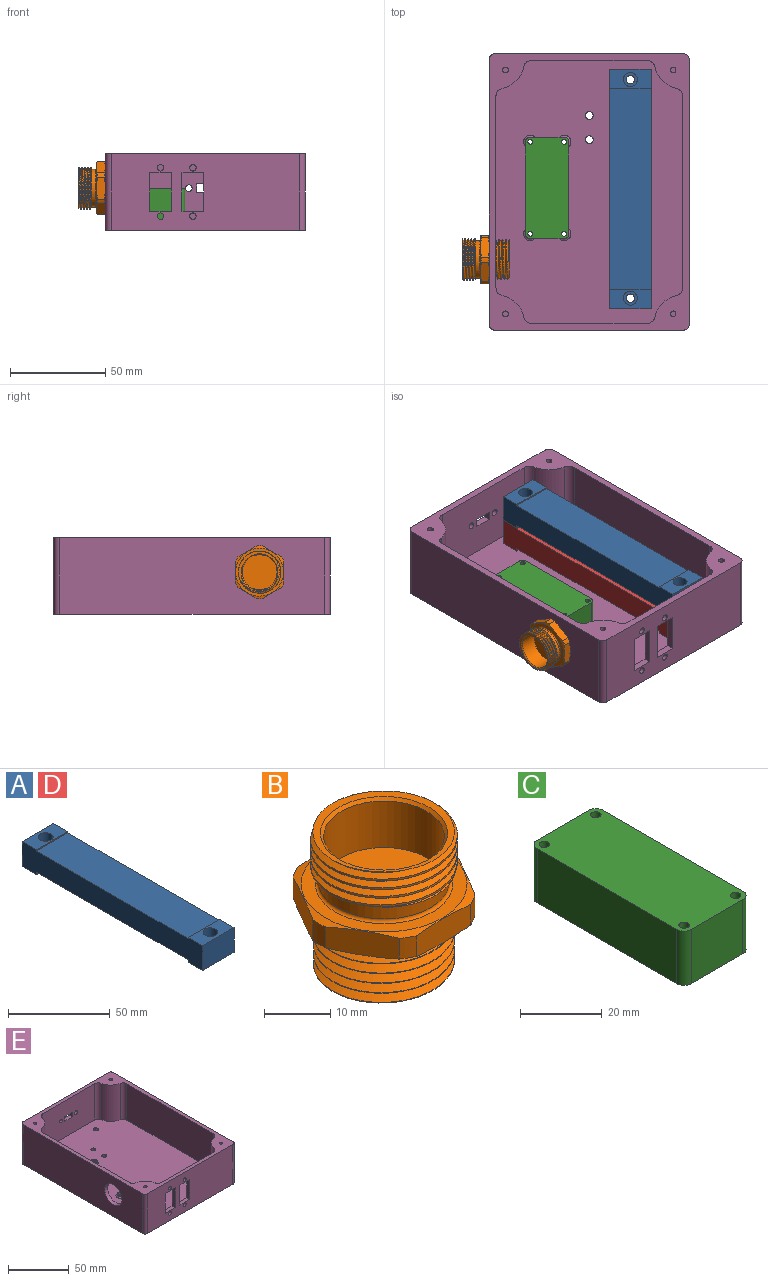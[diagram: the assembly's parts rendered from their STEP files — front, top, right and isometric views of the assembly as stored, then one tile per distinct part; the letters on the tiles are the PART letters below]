
ASSEMBLY  parts=5 mates=3
PART A: 20 faces, bbox 21.9x125.7x15 mm
  f0: plane 21.93x14.95mm, normal (0,-1,0), area 327.9mm2, adj f1,f11,f12,f13
  f1: plane 21.93x10mm, normal (0,0,-1), area 203.7mm2, adj f0,f2,f12,f13,f14
  f2: plane 21.93x1.5mm, normal (0,1,0), area 32.9mm2, adj f1,f3,f12,f13
  f3: plane 105.73x21.93mm, normal (0,0,-1), area 2318.7mm2, adj f2,f4,f12,f13
  f4: plane 21.93x1.5mm, normal (0,-1,0), area 32.9mm2, adj f3,f5,f12,f13
  f5: plane 21.93x10mm, normal (0,0,-1), area 203.7mm2, adj f4,f6,f12,f13,f17
  f6: plane 21.93x14.95mm, normal (0,1,0), area 327.9mm2, adj f5,f7,f12,f13
  f7: plane 21.93x10mm, normal (0,0,1), area 177.4mm2, adj f6,f8,f12,f13,f19
  f8: plane 21.93x0.68mm, normal (0,-1,0), area 14.9mm2, adj f7,f9,f12,f13
  f9: plane 105.73x21.93mm, normal (0,0,1), area 2318.7mm2, adj f8,f10,f12,f13
  f10: plane 21.93x0.68mm, normal (0,1,0), area 14.9mm2, adj f9,f11,f12,f13
  f11: plane 21.93x10mm, normal (0,0,1), area 177.4mm2, adj f0,f10,f12,f13,f16
  f12: plane 125.73x14.95mm, normal (-1,0,0), area 1649.2mm2, adj f0,f1,f2,f3,f4,f5,f6,f7
  f13: plane 125.73x14.95mm, normal (1,0,0), area 1649.2mm2, adj f0,f1,f2,f3,f4,f5,f6,f7
  f14: cylinder r=2.23mm len=4.45mm, axis (0,0,1), area 44mm2, adj f1,f15
  f15: plane 7.3x7.3mm, normal (0,0,1), area 26.3mm2, adj f14,f16
  f16: cylinder r=3.65mm len=11.8mm, axis (0,0,1), area 270.6mm2, adj f11,f15
  f17: cylinder r=2.23mm len=4.45mm, axis (0,0,1), area 44mm2, adj f5,f18
  f18: plane 7.3x7.3mm, normal (0,0,1), area 26.3mm2, adj f17,f19
  f19: cylinder r=3.65mm len=11.8mm, axis (0,0,1), area 270.6mm2, adj f7,f18
PART B: 37 faces, bbox 29x29x27.2 mm
  f0: cone r=9.14mm half-angle=45deg, axis (0,0,1), area 41.7mm2, adj f1,f11
  f1: cylinder r=9.14mm len=18.29mm, axis (0,0,1), area 494.7mm2, adj f0,f36
  f2: torus R=10.42mm, axis (0,0,-1), area 50.8mm2, adj f6,f10
  f3: cone r=12.57mm half-angle=75.1deg, axis (0,0,1), area 58.6mm2, adj f4,f16,f17,f18,f19,f20,f21,f22
  f4: cylinder r=13.97mm len=3.83mm, axis (0,0,1), area 10mm2, adj f3,f5,f18,f19
  f5: cone r=12.57mm half-angle=75.1deg, axis (0,0,-1), area 58.6mm2, adj f4,f10,f16,f17,f18,f19,f20,f21
  f6: cylinder r=9.91mm len=19.81mm, axis (0,0,-1), area 150mm2, adj f2,f15
  f7: cylinder r=11.11mm len=22.23mm, axis (0,0,-1), area 96.2mm2, adj f11,f13,f14,f15
  f8: cylinder r=10.67mm len=21.34mm, axis (0,0,1), area 91mm2, adj f9,f27,f28,f30,f31,f32,f33,f34
  f9: plane 21.1x21.07mm, normal (0,0,-1), area 313.4mm2, adj f8,f28,f29,f30
  f10: plane 25.15x25.15mm, normal (0,0,1), area 156mm2, adj f2,f5
  f11: plane 22.04x22mm, normal (0,0,1), area 67.3mm2, adj f0,f7,f12,f13,f14
  f12: cylinder r=10.16mm len=20.32mm, axis (0,0,-1), area 71.7mm2, adj f11,f13,f14,f15
  f13: bspline ~22.23x22.23mm, area 300.1mm2, adj f7,f11,f12,f15
  f14: bspline ~22.25x22.25mm, area 300.2mm2, adj f7,f11,f12,f15
  f15: plane 22.1x21.92mm, normal (0,0,-1), area 51.3mm2, adj f6,f7,f12,f13,f14
  f16: plane 10.08x5.82mm, normal (-0.87,-0.5,0), area 49.7mm2, adj f3,f5,f23,f26
  f17: plane 11.64x4.51mm, normal (0,-1,0), area 49.8mm2, adj f3,f5,f22,f23
  f18: plane 10.08x5.82mm, normal (0.87,-0.5,0), area 49.8mm2, adj f3,f4,f5,f22
  f19: plane 10.08x5.82mm, normal (0.87,0.5,0), area 49.8mm2, adj f3,f4,f5,f21
  f20: plane 11.64x4.51mm, normal (0,1,0), area 49.8mm2, adj f3,f5,f21,f25
  f21: cylinder r=13.97mm len=3.83mm, axis (0,0,1), area 10mm2, adj f3,f5,f19,f20
  f22: cylinder r=13.97mm len=3.83mm, axis (0,0,1), area 10mm2, adj f3,f5,f17,f18
  f23: cylinder r=13.97mm len=3.83mm, axis (0,0,1), area 10mm2, adj f3,f5,f16,f17
  f24: plane 10.08x5.82mm, normal (-0.87,0.5,0), area 49.8mm2, adj f3,f5,f25,f26
  f25: cylinder r=13.97mm len=3.83mm, axis (0,0,1), area 10mm2, adj f3,f5,f20,f24
  f26: cylinder r=13.97mm len=3.83mm, axis (0,0,1), area 10mm2, adj f3,f5,f16,f24
  f27: plane 25.15x25.15mm, normal (0,0,-1), area 139.2mm2, adj f3,f8,f31,f32,f35
  f28: bspline ~22.43x21.37mm, area 587.3mm2, adj f8,f9,f29,f31
  f29: bspline ~19.37x18.44mm, area 5mm2, adj f9,f28,f30,f33
  f30: bspline ~22.43x21.34mm, area 536.9mm2, adj f8,f9,f29,f34
  f31: plane 4.86x3.84mm, normal (0.34,0.37,-0.87), area 6.2mm2, adj f8,f27,f28,f32,f33,f35
  f32: plane 1.7x0.05mm, normal (-0.71,-0.7,0), area 0.1mm2, adj f8,f27,f31,f34,f35
  f33: plane 3.84x3.81mm, normal (0.71,0.7,-0.01), area 0.1mm2, adj f8,f29,f31,f34
  f34: plane 4.83x3.84mm, normal (0.37,0.34,0.87), area 6.2mm2, adj f8,f30,f32,f33
  f35: cylinder r=10.67mm len=0.75mm, axis (0,0,1), area 0mm2, adj f27,f31,f32
  f36: plane 18.29x18.29mm, normal (0,0,1), area 262.7mm2, adj f1
PART C: 14 faces, bbox 22.9x53.3x16.2 mm
  f0: plane 17.78x16.2mm, normal (0,1,0), area 288mm2, adj f1,f11,f12,f13
  f1: cylinder r=2.54mm len=16.2mm, axis (0,0,-1), area 64.6mm2, adj f0,f2,f12,f13
  f2: plane 48.26x16.2mm, normal (-1,0,0), area 781.8mm2, adj f1,f3,f12,f13
  f3: cylinder r=2.54mm len=16.2mm, axis (0,0,-1), area 64.6mm2, adj f2,f4,f12,f13
  f4: plane 17.78x16.2mm, normal (0,-1,0), area 288mm2, adj f3,f5,f12,f13
  f5: cylinder r=2.54mm len=16.2mm, axis (0,0,-1), area 64.6mm2, adj f4,f6,f12,f13
  f6: plane 48.26x16.2mm, normal (1,0,0), area 781.8mm2, adj f5,f11,f12,f13
  f7: cylinder r=1.27mm len=16.2mm, axis (0,0,-1), area 129.3mm2, adj f12,f13
  f8: cylinder r=1.27mm len=16.2mm, axis (0,0,-1), area 129.3mm2, adj f12,f13
  f9: cylinder r=1.27mm len=16.2mm, axis (0,0,-1), area 129.3mm2, adj f12,f13
  f10: cylinder r=1.27mm len=16.2mm, axis (0,0,-1), area 129.3mm2, adj f12,f13
  f11: cylinder r=2.54mm len=16.2mm, axis (0,0,-1), area 64.6mm2, adj f0,f6,f12,f13
  f12: plane 53.34x22.86mm, normal (0,0,1), area 1193.5mm2, adj f0,f1,f2,f3,f4,f5,f6,f7
  f13: plane 53.34x22.86mm, normal (0,0,-1), area 1193.5mm2, adj f0,f1,f2,f3,f4,f5,f6,f7
PART D: same geometry as A
PART E: 80 faces, bbox 105x145x40 mm
  f0: plane 60.85x36.5mm, normal (0,-1,0), area 2160.7mm2, adj f4,f6,f66,f69,f72,f73,f74,f75
  f1: plane 99x40mm, normal (0,1,0), area 3899.6mm2, adj f6,f10,f16,f17,f72,f73,f74,f75
  f2: plane 60.85x36.5mm, normal (0,1,0), area 1724.8mm2, adj f4,f6,f19,f20,f21,f22,f23,f24
  f3: plane 100.85x36.5mm, normal (-1,0,0), area 3681.1mm2, adj f4,f6,f63,f65
  f4: plane 138x98mm, normal (0,0,1), area 12582.2mm2, adj f0,f2,f3,f5,f11,f13,f32,f35
  f5: plane 100.85x36.5mm, normal (1,0,0), area 3366.9mm2, adj f4,f6,f67,f70,f71
  f6: plane 145x105mm, normal (0,0,1), area 2391.2mm2, adj f0,f1,f2,f3,f5,f7,f8,f9
  f7: plane 99x40mm, normal (0,-1,0), area 3463.7mm2, adj f6,f10,f15,f18,f19,f20,f21,f22
  f8: plane 139x40mm, normal (1,0,0), area 5560mm2, adj f6,f10,f15,f16
  f9: plane 139x40mm, normal (-1,0,0), area 5245.8mm2, adj f6,f10,f17,f18,f71
  f10: plane 145x105mm, normal (0,0,-1), area 14996.6mm2, adj f1,f7,f8,f9,f12,f14,f15,f16
  f11: cylinder r=2.25mm len=4.5mm, axis (0,0,-1), area 11.9mm2, adj f4,f12
  f12: cone r=2.25mm half-angle=41deg, axis (0,0,-1), area 75.3mm2, adj f10,f11
  f13: cylinder r=2.25mm len=4.5mm, axis (0,0,-1), area 11.9mm2, adj f4,f14
  f14: cone r=2.25mm half-angle=41deg, axis (0,0,-1), area 75.3mm2, adj f10,f13
  f15: cylinder r=3mm len=40mm, axis (0,0,1), area 188.5mm2, adj f6,f7,f8,f10
  f16: cylinder r=3mm len=40mm, axis (0,0,-1), area 188.5mm2, adj f1,f6,f8,f10
  f17: cylinder r=3mm len=40mm, axis (0,0,1), area 188.5mm2, adj f1,f6,f9,f10
  f18: cylinder r=3mm len=40mm, axis (0,0,-1), area 188.5mm2, adj f6,f7,f9,f10
  f19: cylinder r=1.7mm len=3.5mm, axis (0,-1,0), area 37.4mm2, adj f2,f7
  f20: cylinder r=1.7mm len=3.5mm, axis (0,-1,0), area 37.4mm2, adj f2,f7
  f21: cylinder r=1.7mm len=3.5mm, axis (0,-1,0), area 37.4mm2, adj f2,f7
  f22: cylinder r=1.7mm len=3.5mm, axis (0,-1,0), area 37.4mm2, adj f2,f7
  f23: plane 11.5x3.5mm, normal (0,0,-1), area 40.3mm2, adj f2,f7,f24,f25
  f24: plane 20x3.5mm, normal (-1,0,0), area 70mm2, adj f2,f7,f23,f26
  f25: plane 20x3.5mm, normal (1,0,0), area 70mm2, adj f2,f7,f23,f26
  f26: plane 11.5x3.5mm, normal (0,0,1), area 40.3mm2, adj f2,f7,f24,f25
  f27: plane 11.5x3.5mm, normal (0,0,-1), area 40.3mm2, adj f2,f7,f28,f29
  f28: plane 20x3.5mm, normal (-1,0,0), area 70mm2, adj f2,f7,f27,f30
  f29: plane 20x3.5mm, normal (1,0,0), area 70mm2, adj f2,f7,f27,f30
  f30: plane 11.5x3.5mm, normal (0,0,1), area 40.3mm2, adj f2,f7,f28,f29
  f31: cylinder r=1.5mm len=36.5mm, axis (0,0,1), area 344mm2, adj f6,f33
  f32: cylinder r=15mm len=36.5mm, axis (0,0,1), area 627.7mm2, adj f4,f6,f69,f70
  f33: plane 3x3mm, normal (0,0,1), area 7.1mm2, adj f31
  f34: cylinder r=1.5mm len=36.5mm, axis (0,0,1), area 344mm2, adj f6,f36
  f35: cylinder r=15mm len=36.5mm, axis (0,0,1), area 627.7mm2, adj f4,f6,f67,f68
  f36: plane 3x3mm, normal (0,0,1), area 7.1mm2, adj f34
  f37: cylinder r=1.5mm len=36.5mm, axis (0,0,1), area 344mm2, adj f6,f39
  f38: cylinder r=15mm len=36.5mm, axis (0,0,1), area 627.7mm2, adj f4,f6,f65,f66
  f39: plane 3x3mm, normal (0,0,1), area 7.1mm2, adj f37
  f40: cylinder r=1.5mm len=36.5mm, axis (0,0,1), area 344mm2, adj f6,f42
  f41: cylinder r=15mm len=36.5mm, axis (0,0,1), area 627.7mm2, adj f4,f6,f63,f64
  f42: plane 3x3mm, normal (0,0,1), area 7.1mm2, adj f40
  f43: cylinder r=2.54mm len=5.08mm, axis (0,0,-1), area 16mm2, adj f44,f51
  f44: plane 5.08x5.08mm, normal (0,0,1), area 13.7mm2, adj f43,f61
  f45: cylinder r=2.54mm len=5.08mm, axis (0,0,-1), area 16mm2, adj f46,f52
  f46: plane 5.08x5.08mm, normal (0,0,1), area 13.7mm2, adj f45,f59
  f47: cylinder r=2.54mm len=5.08mm, axis (0,0,-1), area 16mm2, adj f48,f53
  f48: plane 5.08x5.08mm, normal (0,0,1), area 13.7mm2, adj f47,f57
  f49: cylinder r=2.54mm len=5.08mm, axis (0,0,-1), area 16mm2, adj f50,f54
  f50: plane 5.08x5.08mm, normal (0,0,1), area 13.7mm2, adj f49,f55
  f51: torus R=3.54mm, axis (0,0,1), area 28.7mm2, adj f4,f43
  f52: torus R=3.54mm, axis (0,0,1), area 28.7mm2, adj f4,f45
  f53: torus R=3.54mm, axis (0,0,1), area 28.7mm2, adj f4,f47
  f54: torus R=3.54mm, axis (0,0,1), area 28.7mm2, adj f4,f49
  f55: cylinder r=1.45mm len=4.7mm, axis (0,0,-1), area 42.8mm2, adj f50,f56
  f56: cone r=1.45mm half-angle=45deg, axis (0,0,-1), area 13.2mm2, adj f10,f55
  f57: cylinder r=1.45mm len=4.7mm, axis (0,0,-1), area 42.8mm2, adj f48,f58
  f58: cone r=1.45mm half-angle=45deg, axis (0,0,-1), area 13.2mm2, adj f10,f57
  f59: cylinder r=1.45mm len=4.7mm, axis (0,0,-1), area 42.8mm2, adj f46,f60
  f60: cone r=1.45mm half-angle=45deg, axis (0,0,-1), area 13.2mm2, adj f10,f59
  f61: cylinder r=1.45mm len=4.7mm, axis (0,0,-1), area 42.8mm2, adj f44,f62
  f62: cone r=1.45mm half-angle=45deg, axis (0,0,-1), area 13.2mm2, adj f10,f61
  f63: cylinder r=4mm len=36.5mm, axis (0,0,1), area 198.4mm2, adj f3,f4,f6,f41
  f64: cylinder r=4mm len=36.5mm, axis (0,0,1), area 198.4mm2, adj f2,f4,f6,f41
  f65: cylinder r=4mm len=36.5mm, axis (0,0,1), area 198.4mm2, adj f3,f4,f6,f38
  f66: cylinder r=4mm len=36.5mm, axis (0,0,1), area 198.4mm2, adj f0,f4,f6,f38
  f67: cylinder r=4mm len=36.5mm, axis (0,0,1), area 198.4mm2, adj f4,f5,f6,f35
  f68: cylinder r=4mm len=36.5mm, axis (0,0,1), area 198.4mm2, adj f2,f4,f6,f35
  f69: cylinder r=4mm len=36.5mm, axis (0,0,1), area 198.4mm2, adj f0,f4,f6,f32
  f70: cylinder r=4mm len=36.5mm, axis (0,0,1), area 198.4mm2, adj f4,f5,f6,f32
  f71: cylinder r=10mm len=20mm, axis (-1,0,0), area 219.9mm2, adj f5,f9
  f72: plane 4.55x3.5mm, normal (1,0,0), area 15.9mm2, adj f0,f1,f73,f75
  f73: plane 9.05x3.5mm, normal (0,0,-1), area 31.7mm2, adj f0,f1,f72,f74
  f74: plane 4.55x3.5mm, normal (-1,0,0), area 15.9mm2, adj f0,f1,f73,f75
  f75: plane 9.05x3.5mm, normal (0,0,1), area 31.7mm2, adj f0,f1,f72,f74
  f76: cylinder r=1.75mm len=3.5mm, axis (0,1,0), area 38.5mm2, adj f0,f1
  f77: cylinder r=1.75mm len=3.5mm, axis (0,1,0), area 38.5mm2, adj f0,f1
  f78: cylinder r=2.05mm len=4.1mm, axis (0,0,-1), area 45.1mm2, adj f4,f10
  f79: cylinder r=2.05mm len=4.1mm, axis (0,0,-1), area 45.1mm2, adj f4,f10
PLACE A t=(0,0,14.95)mm
PLACE B rot(axis=(0,-1,0),90deg) t=(-89.57,25.73,22)mm
PLACE C at identity
PLACE D at identity
PLACE E at identity fixed
MATE fastened E.f49 <-> C.f3  axis (0,0,1) through (-63.49,39.28,5.5)mm
MATE fastened A.f14 <-> D.f14  axis (0,0,-1) through (-10.95,5.48,18.45)mm
MATE fastened B.f0 <-> E.f71  axis (-1,0,0) through (-85,25.73,22)mm
